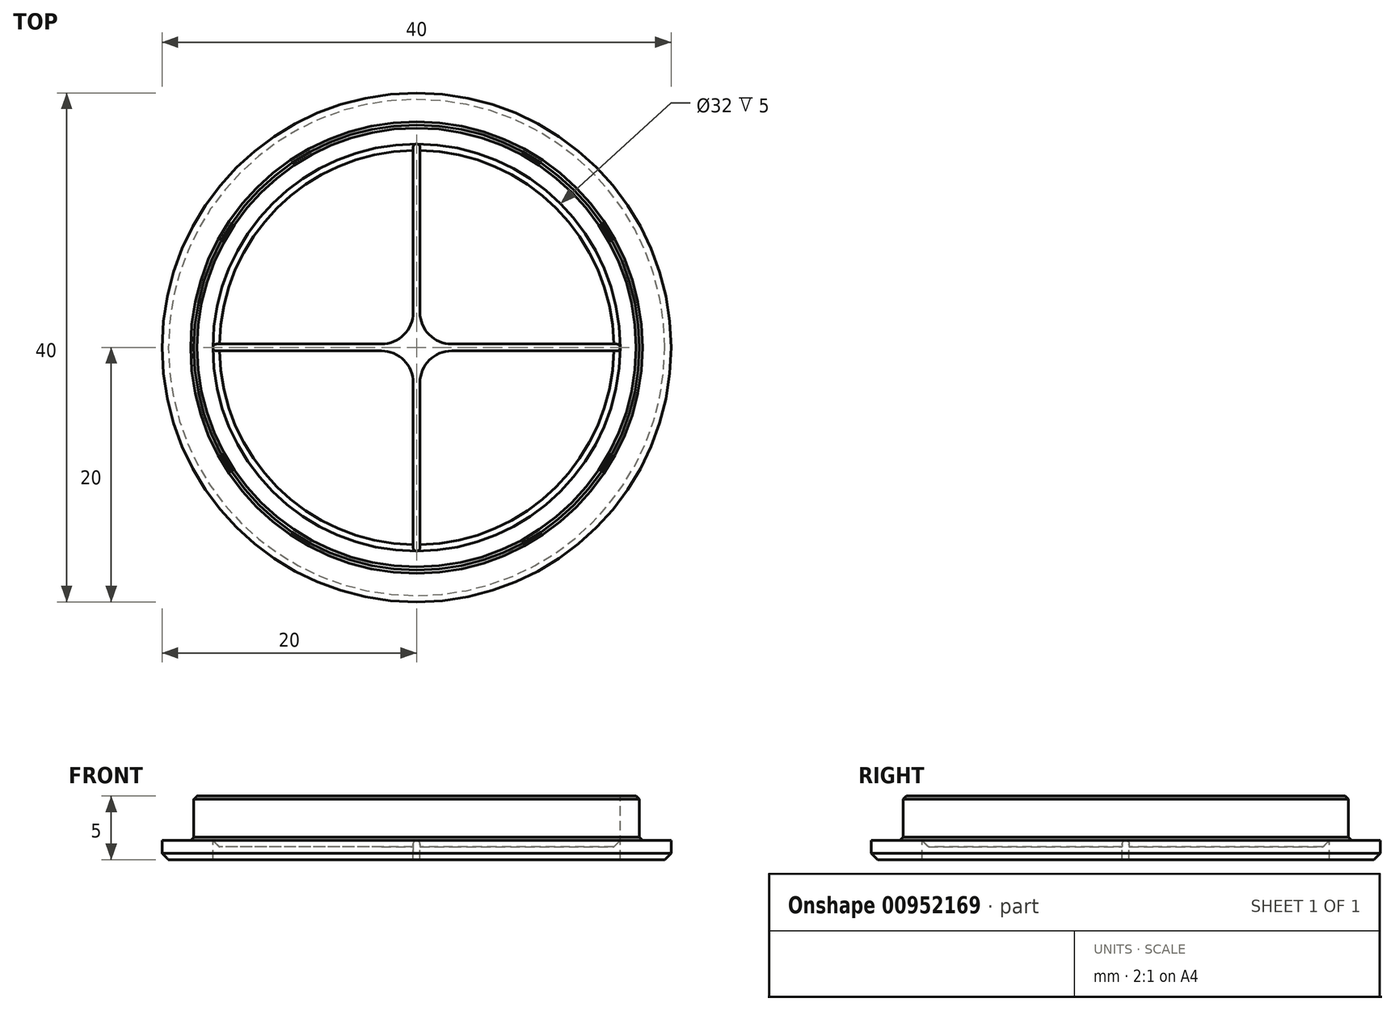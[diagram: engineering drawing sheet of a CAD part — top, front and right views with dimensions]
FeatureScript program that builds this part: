
annotation { "Feature Type Name" : "Feature", "Feature Type Description" : "" }
export const myFeature = defineFeature(function(context is Context, id is Id, definition is map)
    precondition{}
    {
        {
            var Q0;
            Q0=qCreatedBy(makeId("Front.planeOp"),FACE);
            var sketch = newSketch(context, id + "F0", { "sketchPlane" : qUnion([Q0])});
            skLineSegment(sketch, "E0.bottom", {"start": v(0, 0) * mm, "end": v(20, 0) * mm});
            skLineSegment(sketch, "E0.top", {"start": v(0, 5) * mm, "end": v(20, 5) * mm});
            skLineSegment(sketch, "E0.left", {"start": v(0, 0) * mm, "end": v(0, 5) * mm});
            skLineSegment(sketch, "E0.right", {"start": v(20, 0) * mm, "end": v(20, 5) * mm});
            skPoint(sketch, "E1.middle", {"position": v(20, 2.5) * mm});
            skLineSegment(sketch, "E2", {"start": v(17.5, 1.5) * mm, "end": v(17.5, 5) * mm});
            skLineSegment(sketch, "E3", {"start": v(17.5, 1.5) * mm, "end": v(20, 1.5) * mm});
            skSolve(sketch);
        }
        {
            var Q0;
            {var subQ1=sQuery(id+"F0.wireOp",EDGE,"E0.bottom");Q0=makeQuery(id+"F0.imprint","IMPRINT",FACE,{"disambiguationData":[TD([[makeQuery(id+"F0.imprint","IMPRINT",EDGE,{"derivedFrom":subQ1}),1.0]])]});}
            var Q1;
            Q1=sQuery(id+"F0.wireOp",EDGE,"E0.left");
            revolve(context, id + "F1", {"surfaceOperationType" : NewSurfaceOperationType.NEW, "entities" : qUnion([Q0]), "axis" : qUnion([Q1]), "revolveType" : RevolveType.FULL});
        }
        {
            var Q0;
            Q0=makeQuery(id+"F1.opRevolve","SWEPT_FACE",FACE,{"disambiguationData":[OSD([sQuery(id+"F0.wireOp",EDGE,"E0.top")])]});
            var sketch = newSketch(context, id + "F2", { "sketchPlane" : qUnion([Q0])});
            skCircle(sketch, "E4.0", {"center": v(0, 0) * mm, "radius": 16 * mm});
            skLineSegment(sketch, "E5.0", {"start": v(-0.27, -0.27) * mm, "end": v(-0.27, -16) * mm});
            skLineSegment(sketch, "E5.1", {"start": v(-0.27, -0.27) * mm, "end": v(-16, -0.27) * mm});
            skLineSegment(sketch, "E6.0", {"start": v(0.27, -0.27) * mm, "end": v(0.27, -16) * mm});
            skLineSegment(sketch, "E6.1", {"start": v(0.27, -0.27) * mm, "end": v(16, -0.27) * mm});
            skLineSegment(sketch, "E7.0", {"start": v(0.27, 0.27) * mm, "end": v(0.27, 16) * mm});
            skLineSegment(sketch, "E7.1", {"start": v(0.27, 0.27) * mm, "end": v(16, 0.27) * mm});
            skLineSegment(sketch, "E8.0", {"start": v(-0.27, 0.27) * mm, "end": v(-0.27, 16) * mm});
            skLineSegment(sketch, "E8.1", {"start": v(-0.27, 0.27) * mm, "end": v(-16, 0.27) * mm});
            skSolve(sketch);
        }
        {
            var Q0;
            {var subQ3=sQuery(id+"F2.wireOp",EDGE,"E4.0");var subQ10=makeQuery(id+"F2.imprint","INTERSECT",VERTEX,{"derivedFrom":[subQ3,sQuery(id+"F2.wireOp",EDGE,"cabae8e6-8054-485d-9847-b452425a3894.trimOffspring")]});Q0=makeQuery(id+"F2.imprint","IMPRINT",FACE,{"disambiguationData":[TD([[makeQuery(id+"F2.imprint","IMPRINT",EDGE,{"disambiguationData":[TD([[subQ10,-1.0]])],"derivedFrom":subQ3}),1.0]])]});}
            extrude(context, id + "F3", {"entities" : qUnion([Q0]), "operationType" : NewBodyOperationType.REMOVE, "oppositeDirection" : true, "depth" : 12.4 * mm, "offsetDistance" : 25 * mm});
        }
        {
            var Q0;
            {var subQ0=sQuery(id+"F2.wireOp",EDGE,"E7.1");var subQ1=sQuery(id+"F2.wireOp",EDGE,"E4.0");var subQ2=makeQuery(id+"F2.imprint","INTERSECT",VERTEX,{"derivedFrom":[subQ1,subQ0]});Q0=makeQuery(id+"F2.imprint","IMPRINT",FACE,{"disambiguationData":[TD([[makeQuery(id+"F2.imprint","IMPRINT",EDGE,{"disambiguationData":[TD([[subQ2,-1.0]])],"derivedFrom":subQ1}),1.0]])]});}
            var Q1;
            {var subQ0=sQuery(id+"F2.wireOp",EDGE,"E8.0");var subQ1=sQuery(id+"F2.wireOp",EDGE,"E4.0");var subQ2=makeQuery(id+"F2.imprint","INTERSECT",VERTEX,{"derivedFrom":[subQ1,subQ0]});Q1=makeQuery(id+"F2.imprint","IMPRINT",FACE,{"disambiguationData":[TD([[makeQuery(id+"F2.imprint","IMPRINT",EDGE,{"disambiguationData":[TD([[subQ2,-1.0]])],"derivedFrom":subQ1}),1.0]])]});}
            var Q2;
            {var subQ0=sQuery(id+"F2.wireOp",EDGE,"E6.0");var subQ1=sQuery(id+"F2.wireOp",EDGE,"E4.0");var subQ2=makeQuery(id+"F2.imprint","INTERSECT",VERTEX,{"derivedFrom":[subQ1,subQ0]});Q2=makeQuery(id+"F2.imprint","IMPRINT",FACE,{"disambiguationData":[TD([[makeQuery(id+"F2.imprint","IMPRINT",EDGE,{"disambiguationData":[TD([[subQ2,-1.0]])],"derivedFrom":subQ1}),1.0]])]});}
            var Q3;
            {var subQ0=sQuery(id+"F2.wireOp",EDGE,"E5.1");var subQ1=sQuery(id+"F2.wireOp",EDGE,"E4.0");var subQ2=makeQuery(id+"F2.imprint","INTERSECT",VERTEX,{"derivedFrom":[subQ1,subQ0]});Q3=makeQuery(id+"F2.imprint","IMPRINT",FACE,{"disambiguationData":[TD([[makeQuery(id+"F2.imprint","IMPRINT",EDGE,{"disambiguationData":[TD([[subQ2,-1.0]])],"derivedFrom":subQ1}),1.0]])]});}
            extrude(context, id + "F4", {"entities" : qUnion([Q0, Q1, Q2, Q3]), "operationType" : NewBodyOperationType.REMOVE, "oppositeDirection" : true, "depth" : 4 * mm, "offsetDistance" : 25 * mm});
        }
        {
            var Q0;
            Q0=makeQuery(id+"F1.opRevolve","SWEPT_EDGE",EDGE,{"disambiguationData":[OSD([sQuery(id+"F0.wireOp",EDGE,"E1.top"),sQuery(id+"F0.wireOp",EDGE,"E1.right")])]});
            var Q1;
            Q1=makeQuery(id+"F1.opRevolve","SWEPT_EDGE",EDGE,{"disambiguationData":[OSD([sQuery(id+"F0.wireOp",EDGE,"E1.bottom"),sQuery(id+"F0.wireOp",EDGE,"E1.right")])]});
            var Q2;
            Q2=makeQuery(id+"F1.opRevolve","SWEPT_EDGE",EDGE,{"disambiguationData":[OSD([sQuery(id+"F0.wireOp",EDGE,"E0.bottom"),sQuery(id+"F0.wireOp",EDGE,"E0.right")])]});
            var Q3;
            {var subQ0=sQuery(id+"F2.wireOp",EDGE,"E4.0");Q3=makeQuery(id+"F4.boolean.opBoolean","COPY",EDGE,{"derivedFrom":makeQuery(id+"F4.opExtrude","CAP_EDGE",EDGE,{"disambiguationData":[OSD([subQ0]),TDD([makeQuery(id+"F2.imprint","IMPRINT",EDGE,{"disambiguationData":[TD([[makeQuery(id+"F2.imprint","INTERSECT",VERTEX,{"derivedFrom":[subQ0,sQuery(id+"F2.wireOp",EDGE,"E6.0")]}),-1.0]])],"derivedFrom":subQ0})])],"isStart":false})});}
            var Q4;
            {var subQ0=sQuery(id+"F2.wireOp",EDGE,"E4.0");Q4=makeQuery(id+"F4.boolean.opBoolean","COPY",EDGE,{"derivedFrom":makeQuery(id+"F4.opExtrude","CAP_EDGE",EDGE,{"disambiguationData":[OSD([subQ0]),TDD([makeQuery(id+"F2.imprint","IMPRINT",EDGE,{"disambiguationData":[TD([[makeQuery(id+"F2.imprint","INTERSECT",VERTEX,{"derivedFrom":[subQ0,sQuery(id+"F2.wireOp",EDGE,"E5.1")]}),-1.0]])],"derivedFrom":subQ0})])],"isStart":false})});}
            var Q5;
            {var subQ0=sQuery(id+"F2.wireOp",EDGE,"E4.0");Q5=makeQuery(id+"F4.boolean.opBoolean","COPY",EDGE,{"derivedFrom":makeQuery(id+"F4.opExtrude","CAP_EDGE",EDGE,{"disambiguationData":[OSD([subQ0]),TDD([makeQuery(id+"F2.imprint","IMPRINT",EDGE,{"disambiguationData":[TD([[makeQuery(id+"F2.imprint","INTERSECT",VERTEX,{"derivedFrom":[subQ0,sQuery(id+"F2.wireOp",EDGE,"E8.0")]}),-1.0]])],"derivedFrom":subQ0})])],"isStart":false})});}
            var Q6;
            {var subQ0=sQuery(id+"F2.wireOp",EDGE,"E4.0");Q6=makeQuery(id+"F4.boolean.opBoolean","COPY",EDGE,{"derivedFrom":makeQuery(id+"F4.opExtrude","CAP_EDGE",EDGE,{"disambiguationData":[OSD([subQ0]),TDD([makeQuery(id+"F2.imprint","IMPRINT",EDGE,{"disambiguationData":[TD([[makeQuery(id+"F2.imprint","INTERSECT",VERTEX,{"derivedFrom":[subQ0,sQuery(id+"F2.wireOp",EDGE,"E7.1")]}),-1.0]])],"derivedFrom":subQ0})])],"isStart":false})});}
            var Q7;
            Q7=makeQuery(id+"F1.opRevolve","SWEPT_EDGE",EDGE,{"disambiguationData":[OSD([sQuery(id+"F0.wireOp",EDGE,"E0.bottom"),sQuery(id+"F0.wireOp",EDGE,"E0.right")])]});
            var Q8;
            Q8=makeQuery(id+"F1.opRevolve","SWEPT_EDGE",EDGE,{"disambiguationData":[OSD([sQuery(id+"F0.wireOp",EDGE,"E0.bottom"),sQuery(id+"F0.wireOp",EDGE,"E0.right")])]});
            chamfer(context, id + "F5", {"entities" : qUnion([Q0, Q1, Q2, Q3, Q4, Q5, Q6, Q7, Q8]), "width" : 0.5 * mm, "tangentPropagation" : true});
        }
        {
            var Q0;
            Q0=makeQuery(id+"F3.boolean.opBoolean","COPY",EDGE,{"derivedFrom":makeQuery(id+"F3.opExtrude","SWEPT_EDGE",EDGE,{"disambiguationData":[OSD([sQuery(id+"F2.wireOp",EDGE,"E8.0"),sQuery(id+"F2.wireOp",EDGE,"E8.1")])]})});
            var Q1;
            Q1=makeQuery(id+"F3.boolean.opBoolean","COPY",EDGE,{"derivedFrom":makeQuery(id+"F3.opExtrude","SWEPT_EDGE",EDGE,{"disambiguationData":[OSD([sQuery(id+"F2.wireOp",EDGE,"E5.0"),sQuery(id+"F2.wireOp",EDGE,"E5.1")])]})});
            var Q2;
            Q2=makeQuery(id+"F3.boolean.opBoolean","COPY",EDGE,{"derivedFrom":makeQuery(id+"F3.opExtrude","SWEPT_EDGE",EDGE,{"disambiguationData":[OSD([sQuery(id+"F2.wireOp",EDGE,"E6.0"),sQuery(id+"F2.wireOp",EDGE,"E6.1")])]})});
            var Q3;
            Q3=makeQuery(id+"F3.boolean.opBoolean","COPY",EDGE,{"derivedFrom":makeQuery(id+"F3.opExtrude","SWEPT_EDGE",EDGE,{"disambiguationData":[OSD([sQuery(id+"F2.wireOp",EDGE,"E7.0"),sQuery(id+"F2.wireOp",EDGE,"E7.1")])]})});
            fillet(context, id + "F6", {"entities" : qUnion([Q0, Q1, Q2, Q3]), "radius" : 2.5 * mm, "tangentPropagation" : true, "allowEdgeOverflow" : false});
        }
        {
            var Q0;
            Q0=makeQuery(id+"F1.opRevolve","SWEPT_EDGE",EDGE,{"disambiguationData":[OSD([sQuery(id+"F0.wireOp",EDGE,"E0.top"),sQuery(id+"F0.wireOp",EDGE,"E2")])]});
            var Q1;
            {var subQ0=sQuery(id+"F2.wireOp",EDGE,"E4.0");var subQ1=makeQuery(id+"F2.imprint","INTERSECT",VERTEX,{"derivedFrom":[subQ0,sQuery(id+"F2.wireOp",EDGE,"E6.0")]});var subQ3=makeQuery(id+"F2.imprint","INTERSECT",VERTEX,{"derivedFrom":[subQ0,sQuery(id+"F2.wireOp",EDGE,"E5.1")]});var subQ4=makeQuery(id+"F2.imprint","INTERSECT",VERTEX,{"derivedFrom":[subQ0,sQuery(id+"F2.wireOp",EDGE,"E5.0")]});var subQ5=makeQuery(id+"F2.imprint","INTERSECT",VERTEX,{"derivedFrom":[subQ0,sQuery(id+"F2.wireOp",EDGE,"E8.0")]});var subQ6=makeQuery(id+"F2.imprint","INTERSECT",VERTEX,{"derivedFrom":[subQ0,sQuery(id+"F2.wireOp",EDGE,"E8.1")]});var subQ7=makeQuery(id+"F2.imprint","INTERSECT",VERTEX,{"derivedFrom":[subQ0,sQuery(id+"F2.wireOp",EDGE,"E7.0")]});var subQ8=makeQuery(id+"F2.imprint","INTERSECT",VERTEX,{"derivedFrom":[subQ0,sQuery(id+"F2.wireOp",EDGE,"E7.1")]});Q1=makeQuery(id+"F4.boolean.opBoolean","MERGE",EDGE,{"derivedFrom":[makeQuery(id+"F3.boolean.opBoolean","COPY",EDGE,{"derivedFrom":makeQuery(id+"F3.opExtrude","CAP_EDGE",EDGE,{"disambiguationData":[OSD([subQ0]),TDD([makeQuery(id+"F2.imprint","IMPRINT",EDGE,{"disambiguationData":[TD([[subQ7,-1.0]])],"derivedFrom":subQ0})])],"isStart":true})}),makeQuery(id+"F3.boolean.opBoolean","COPY",EDGE,{"derivedFrom":makeQuery(id+"F3.opExtrude","CAP_EDGE",EDGE,{"disambiguationData":[OSD([subQ0]),TDD([makeQuery(id+"F2.imprint","IMPRINT",EDGE,{"disambiguationData":[TD([[subQ6,-1.0]])],"derivedFrom":subQ0})])],"isStart":true})}),makeQuery(id+"F3.boolean.opBoolean","COPY",EDGE,{"derivedFrom":makeQuery(id+"F3.opExtrude","CAP_EDGE",EDGE,{"disambiguationData":[OSD([subQ0]),TDD([makeQuery(id+"F2.imprint","IMPRINT",EDGE,{"disambiguationData":[TD([[subQ4,-1.0]])],"derivedFrom":subQ0})])],"isStart":true})}),makeQuery(id+"F3.boolean.opBoolean","COPY",EDGE,{"derivedFrom":makeQuery(id+"F3.opExtrude","CAP_EDGE",EDGE,{"disambiguationData":[OSD([subQ0]),TDD([makeQuery(id+"F2.imprint","IMPRINT",EDGE,{"disambiguationData":[TD([[subQ8,1.0]])],"derivedFrom":subQ0})])],"isStart":true})})],"fromTools":[makeQuery(id+"F4.opExtrude","CAP_EDGE",EDGE,{"disambiguationData":[OSD([subQ0]),TDD([makeQuery(id+"F2.imprint","IMPRINT",EDGE,{"disambiguationData":[TD([[subQ7,1.0]])],"derivedFrom":subQ0})])],"isStart":true}),makeQuery(id+"F4.opExtrude","CAP_EDGE",EDGE,{"disambiguationData":[OSD([subQ0]),TDD([makeQuery(id+"F2.imprint","IMPRINT",EDGE,{"disambiguationData":[TD([[subQ5,-1.0]])],"derivedFrom":subQ0})])],"isStart":true}),makeQuery(id+"F4.opExtrude","CAP_EDGE",EDGE,{"disambiguationData":[OSD([subQ0]),TDD([makeQuery(id+"F2.imprint","IMPRINT",EDGE,{"disambiguationData":[TD([[subQ3,-1.0]])],"derivedFrom":subQ0})])],"isStart":true}),makeQuery(id+"F4.opExtrude","CAP_EDGE",EDGE,{"disambiguationData":[OSD([subQ0]),TDD([makeQuery(id+"F2.imprint","IMPRINT",EDGE,{"disambiguationData":[TD([[subQ1,-1.0]])],"derivedFrom":subQ0})])],"isStart":true})]});}
            var Q2;
            Q2=makeQuery(id+"F1.opRevolve","SWEPT_EDGE",EDGE,{"disambiguationData":[OSD([sQuery(id+"F0.wireOp",EDGE,"E2"),sQuery(id+"F0.wireOp",EDGE,"E3")])]});
            chamfer(context, id + "F7", {"entities" : qUnion([Q0, Q1, Q2]), "width" : .25 * mm, "tangentPropagation" : true});
        }
        {
            var Q0;
            Q0=makeQuery(id+"F3.boolean.opBoolean","COPY",EDGE,{"derivedFrom":makeQuery(id+"F3.opExtrude","SWEPT_EDGE",EDGE,{"disambiguationData":[OSD([sQuery(id+"F2.wireOp",EDGE,"E4.0"),sQuery(id+"F2.wireOp",EDGE,"E6.0")])]})});
            var Q1;
            Q1=makeQuery(id+"F3.boolean.opBoolean","COPY",EDGE,{"derivedFrom":makeQuery(id+"F3.opExtrude","SWEPT_EDGE",EDGE,{"disambiguationData":[OSD([sQuery(id+"F2.wireOp",EDGE,"E4.0"),sQuery(id+"F2.wireOp",EDGE,"E5.0")])]})});
            var Q2;
            Q2=makeQuery(id+"F3.boolean.opBoolean","COPY",EDGE,{"derivedFrom":makeQuery(id+"F3.opExtrude","SWEPT_EDGE",EDGE,{"disambiguationData":[OSD([sQuery(id+"F2.wireOp",EDGE,"E4.0"),sQuery(id+"F2.wireOp",EDGE,"E8.1")])]})});
            var Q3;
            Q3=makeQuery(id+"F3.boolean.opBoolean","COPY",EDGE,{"derivedFrom":makeQuery(id+"F3.opExtrude","SWEPT_EDGE",EDGE,{"disambiguationData":[OSD([sQuery(id+"F2.wireOp",EDGE,"E4.0"),sQuery(id+"F2.wireOp",EDGE,"E5.1")])]})});
            var Q4;
            Q4=makeQuery(id+"F3.boolean.opBoolean","COPY",EDGE,{"derivedFrom":makeQuery(id+"F3.opExtrude","SWEPT_EDGE",EDGE,{"disambiguationData":[OSD([sQuery(id+"F2.wireOp",EDGE,"E4.0"),sQuery(id+"F2.wireOp",EDGE,"E7.0")])]})});
            var Q5;
            Q5=makeQuery(id+"F3.boolean.opBoolean","COPY",EDGE,{"derivedFrom":makeQuery(id+"F3.opExtrude","SWEPT_EDGE",EDGE,{"disambiguationData":[OSD([sQuery(id+"F2.wireOp",EDGE,"E4.0"),sQuery(id+"F2.wireOp",EDGE,"E8.0")])]})});
            var Q6;
            Q6=makeQuery(id+"F3.boolean.opBoolean","COPY",EDGE,{"derivedFrom":makeQuery(id+"F3.opExtrude","SWEPT_EDGE",EDGE,{"disambiguationData":[OSD([sQuery(id+"F2.wireOp",EDGE,"E4.0"),sQuery(id+"F2.wireOp",EDGE,"E7.1")])]})});
            var Q7;
            Q7=makeQuery(id+"F3.boolean.opBoolean","COPY",EDGE,{"derivedFrom":makeQuery(id+"F3.opExtrude","SWEPT_EDGE",EDGE,{"disambiguationData":[OSD([sQuery(id+"F2.wireOp",EDGE,"E4.0"),sQuery(id+"F2.wireOp",EDGE,"E6.1")])]})});
            fillet(context, id + "F8", {"entities" : qUnion([Q0, Q1, Q2, Q3, Q4, Q5, Q6, Q7]), "radius" : 0.27 * mm, "tangentPropagation" : true, "allowEdgeOverflow" : false});
        }
    });
